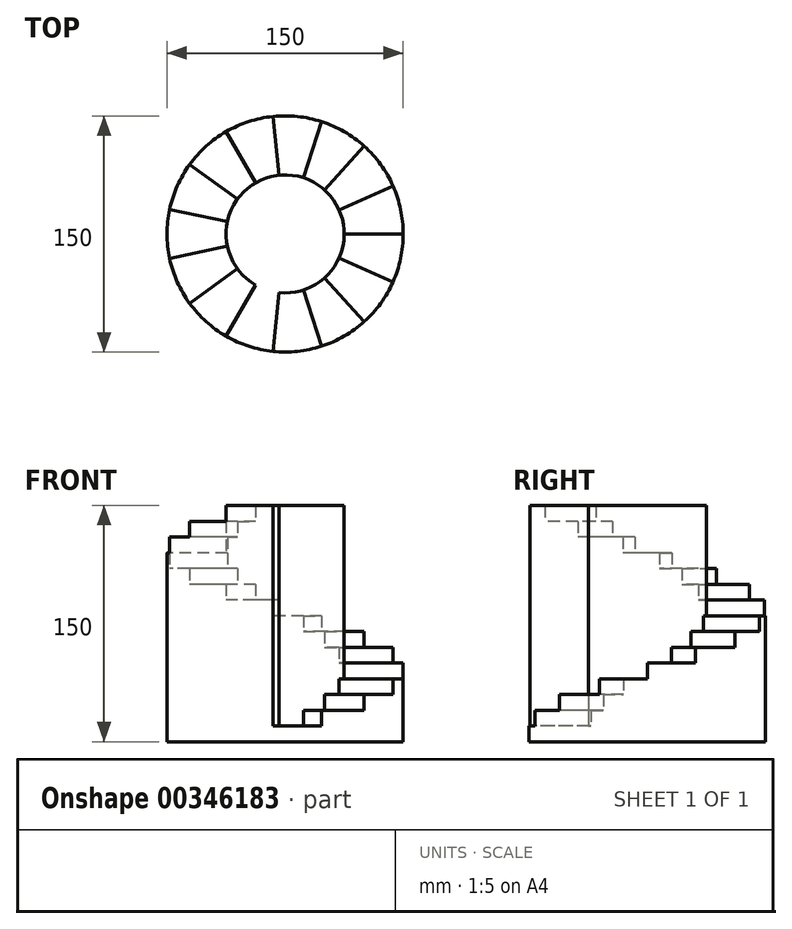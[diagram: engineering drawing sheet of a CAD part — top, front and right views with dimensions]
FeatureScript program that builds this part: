
annotation { "Feature Type Name" : "Feature", "Feature Type Description" : "" }
export const myFeature = defineFeature(function(context is Context, id is Id, definition is map)
    precondition{}
    {
        {
            var Q0;
            Q0=qCreatedBy(makeId("Top.planeOp"),FACE);
            var sketch = newSketch(context, id + "F0", { "sketchPlane" : qUnion([Q0])});
            skCircle(sketch, "E0", {"center": v(0, 0) * mm, "radius": 75 * mm});
            skCircle(sketch, "E1", {"center": v(0, 0) * mm, "radius": 37.5 * mm});
            skLineSegment(sketch, "E2", {"start": v(37.5, 0) * mm, "end": v(75, 0) * mm});
            skLineSegment(sketch, "E3.1.0", {"start": v(34.26, 15.25) * mm, "end": v(68.52, 30.5) * mm});
            skLineSegment(sketch, "E3.2.0", {"start": v(25.1, 27.87) * mm, "end": v(50.18, 55.74) * mm});
            skLineSegment(sketch, "E3.3.0", {"start": v(11.59, 35.66) * mm, "end": v(23.18, 71.33) * mm});
            skLineSegment(sketch, "E3.4.0", {"start": v(-3.92, 37.3) * mm, "end": v(-7.84, 74.59) * mm});
            skLineSegment(sketch, "E3.5.0", {"start": v(-18.75, 32.48) * mm, "end": v(-37.5, 64.95) * mm});
            skLineSegment(sketch, "E3.6.0", {"start": v(-30.34, 22.04) * mm, "end": v(-60.68, 44.08) * mm});
            skLineSegment(sketch, "E3.7.0", {"start": v(-36.68, 7.8) * mm, "end": v(-73.36, 15.6) * mm});
            skLineSegment(sketch, "E3.8.0", {"start": v(-36.68, -7.8) * mm, "end": v(-73.36, -15.6) * mm});
            skLineSegment(sketch, "E3.9.0", {"start": v(-30.34, -22.04) * mm, "end": v(-60.68, -44.08) * mm});
            skLineSegment(sketch, "E3.10.0", {"start": v(-18.75, -32.48) * mm, "end": v(-37.5, -64.95) * mm});
            skLineSegment(sketch, "E3.11.0", {"start": v(-3.92, -37.3) * mm, "end": v(-7.84, -74.59) * mm});
            skLineSegment(sketch, "E3.12.0", {"start": v(11.59, -35.66) * mm, "end": v(23.18, -71.33) * mm});
            skLineSegment(sketch, "E3.13.0", {"start": v(25.1, -27.87) * mm, "end": v(50.18, -55.74) * mm});
            skLineSegment(sketch, "E3.14.0", {"start": v(34.26, -15.25) * mm, "end": v(68.52, -30.5) * mm});
            skSolve(sketch);
        }
        {
            var Q0;
            {var subQ0=sQuery(id+"F0.wireOp",EDGE,"E1");var subQ8=makeQuery(id+"F0.imprint","INTERSECT",VERTEX,{"derivedFrom":[subQ0,sQuery(id+"F0.wireOp",EDGE,"E2")]});Q0=makeQuery(id+"F0.imprint","IMPRINT",FACE,{"disambiguationData":[TD([[makeQuery(id+"F0.imprint","IMPRINT",EDGE,{"disambiguationData":[TD([[subQ8,-1.0]])],"derivedFrom":subQ0}),1.0]])]});}
            extrude(context, id + "F1", {"entities" : qUnion([Q0]), "depth" : 150 * mm});
        }
        {
            var Q0;
            {var subQ0=sQuery(id+"F0.wireOp",EDGE,"E3.11.0");Q0=makeQuery(id+"F0.imprint","IMPRINT",FACE,{"disambiguationData":[TD([[makeQuery(id+"F0.imprint","IMPRINT",EDGE,{"derivedFrom":subQ0}),1.0]])]});}
            extrude(context, id + "F2", {"entities" : qUnion([Q0]), "operationType" : NewBodyOperationType.ADD, "depth" : 10 * mm});
        }
        {
            var Q0;
            {var subQ0=sQuery(id+"F0.wireOp",EDGE,"E3.12.0");Q0=makeQuery(id+"F0.imprint","IMPRINT",FACE,{"disambiguationData":[TD([[makeQuery(id+"F0.imprint","IMPRINT",EDGE,{"derivedFrom":subQ0}),1.0]])]});}
            extrude(context, id + "F3", {"entities" : qUnion([Q0]), "operationType" : NewBodyOperationType.ADD, "depth" : 20 * mm});
        }
        {
            var Q0;
            {var subQ0=sQuery(id+"F0.wireOp",EDGE,"E3.13.0");Q0=makeQuery(id+"F0.imprint","IMPRINT",FACE,{"disambiguationData":[TD([[makeQuery(id+"F0.imprint","IMPRINT",EDGE,{"derivedFrom":subQ0}),1.0]])]});}
            extrude(context, id + "F4", {"entities" : qUnion([Q0]), "operationType" : NewBodyOperationType.ADD, "depth" : 30 * mm});
        }
        {
            var Q0;
            {var subQ0=sQuery(id+"F0.wireOp",EDGE,"E2");Q0=makeQuery(id+"F0.imprint","IMPRINT",FACE,{"disambiguationData":[TD([[makeQuery(id+"F0.imprint","IMPRINT",EDGE,{"derivedFrom":subQ0}),-1.0]])]});}
            extrude(context, id + "F5", {"entities" : qUnion([Q0]), "operationType" : NewBodyOperationType.ADD, "depth" : 40 * mm});
        }
        {
            var Q0;
            {var subQ0=sQuery(id+"F0.wireOp",EDGE,"E2");Q0=makeQuery(id+"F0.imprint","IMPRINT",FACE,{"disambiguationData":[TD([[makeQuery(id+"F0.imprint","IMPRINT",EDGE,{"derivedFrom":subQ0}),1.0]])]});}
            extrude(context, id + "F6", {"entities" : qUnion([Q0]), "operationType" : NewBodyOperationType.ADD, "depth" : 50 * mm});
        }
        {
            var Q0;
            {var subQ0=sQuery(id+"F0.wireOp",EDGE,"E3.1.0");Q0=makeQuery(id+"F0.imprint","IMPRINT",FACE,{"disambiguationData":[TD([[makeQuery(id+"F0.imprint","IMPRINT",EDGE,{"derivedFrom":subQ0}),1.0]])]});}
            extrude(context, id + "F7", {"entities" : qUnion([Q0]), "operationType" : NewBodyOperationType.ADD, "depth" : 60 * mm});
        }
        {
            var Q0;
            {var subQ0=sQuery(id+"F0.wireOp",EDGE,"E3.2.0");Q0=makeQuery(id+"F0.imprint","IMPRINT",FACE,{"disambiguationData":[TD([[makeQuery(id+"F0.imprint","IMPRINT",EDGE,{"derivedFrom":subQ0}),1.0]])]});}
            extrude(context, id + "F8", {"entities" : qUnion([Q0]), "operationType" : NewBodyOperationType.ADD, "depth" : 70 * mm});
        }
        {
            var Q0;
            {var subQ0=sQuery(id+"F0.wireOp",EDGE,"E3.3.0");Q0=makeQuery(id+"F0.imprint","IMPRINT",FACE,{"disambiguationData":[TD([[makeQuery(id+"F0.imprint","IMPRINT",EDGE,{"derivedFrom":subQ0}),1.0]])]});}
            extrude(context, id + "F9", {"entities" : qUnion([Q0]), "operationType" : NewBodyOperationType.ADD, "depth" : 80 * mm});
        }
        {
            var Q0;
            {var subQ0=sQuery(id+"F0.wireOp",EDGE,"E3.4.0");Q0=makeQuery(id+"F0.imprint","IMPRINT",FACE,{"disambiguationData":[TD([[makeQuery(id+"F0.imprint","IMPRINT",EDGE,{"derivedFrom":subQ0}),1.0]])]});}
            extrude(context, id + "F10", {"entities" : qUnion([Q0]), "operationType" : NewBodyOperationType.ADD, "depth" : 90 * mm});
        }
        {
            var Q0;
            {var subQ0=sQuery(id+"F0.wireOp",EDGE,"E3.5.0");Q0=makeQuery(id+"F0.imprint","IMPRINT",FACE,{"disambiguationData":[TD([[makeQuery(id+"F0.imprint","IMPRINT",EDGE,{"derivedFrom":subQ0}),1.0]])]});}
            extrude(context, id + "F11", {"entities" : qUnion([Q0]), "operationType" : NewBodyOperationType.ADD, "depth" : 100 * mm});
        }
        {
            var Q0;
            {var subQ0=sQuery(id+"F0.wireOp",EDGE,"E3.6.0");Q0=makeQuery(id+"F0.imprint","IMPRINT",FACE,{"disambiguationData":[TD([[makeQuery(id+"F0.imprint","IMPRINT",EDGE,{"derivedFrom":subQ0}),1.0]])]});}
            extrude(context, id + "F12", {"entities" : qUnion([Q0]), "operationType" : NewBodyOperationType.ADD, "depth" : 110 * mm});
        }
        {
            var Q0;
            {var subQ0=sQuery(id+"F0.wireOp",EDGE,"E3.7.0");Q0=makeQuery(id+"F0.imprint","IMPRINT",FACE,{"disambiguationData":[TD([[makeQuery(id+"F0.imprint","IMPRINT",EDGE,{"derivedFrom":subQ0}),1.0]])]});}
            extrude(context, id + "F13", {"entities" : qUnion([Q0]), "operationType" : NewBodyOperationType.ADD, "depth" : 120 * mm});
        }
        {
            var Q0;
            {var subQ0=sQuery(id+"F0.wireOp",EDGE,"E3.8.0");Q0=makeQuery(id+"F0.imprint","IMPRINT",FACE,{"disambiguationData":[TD([[makeQuery(id+"F0.imprint","IMPRINT",EDGE,{"derivedFrom":subQ0}),1.0]])]});}
            extrude(context, id + "F14", {"entities" : qUnion([Q0]), "operationType" : NewBodyOperationType.ADD, "depth" : 130 * mm});
        }
        {
            var Q0;
            {var subQ0=sQuery(id+"F0.wireOp",EDGE,"E3.9.0");Q0=makeQuery(id+"F0.imprint","IMPRINT",FACE,{"disambiguationData":[TD([[makeQuery(id+"F0.imprint","IMPRINT",EDGE,{"derivedFrom":subQ0}),1.0]])]});}
            extrude(context, id + "F15", {"entities" : qUnion([Q0]), "operationType" : NewBodyOperationType.ADD, "depth" : 140 * mm});
        }
        {
            var Q0;
            {var subQ0=sQuery(id+"F0.wireOp",EDGE,"E3.10.0");Q0=makeQuery(id+"F0.imprint","IMPRINT",FACE,{"disambiguationData":[TD([[makeQuery(id+"F0.imprint","IMPRINT",EDGE,{"derivedFrom":subQ0}),1.0]])]});}
            extrude(context, id + "F16", {"entities" : qUnion([Q0]), "operationType" : NewBodyOperationType.ADD, "depth" : 150 * mm});
        }
    });
